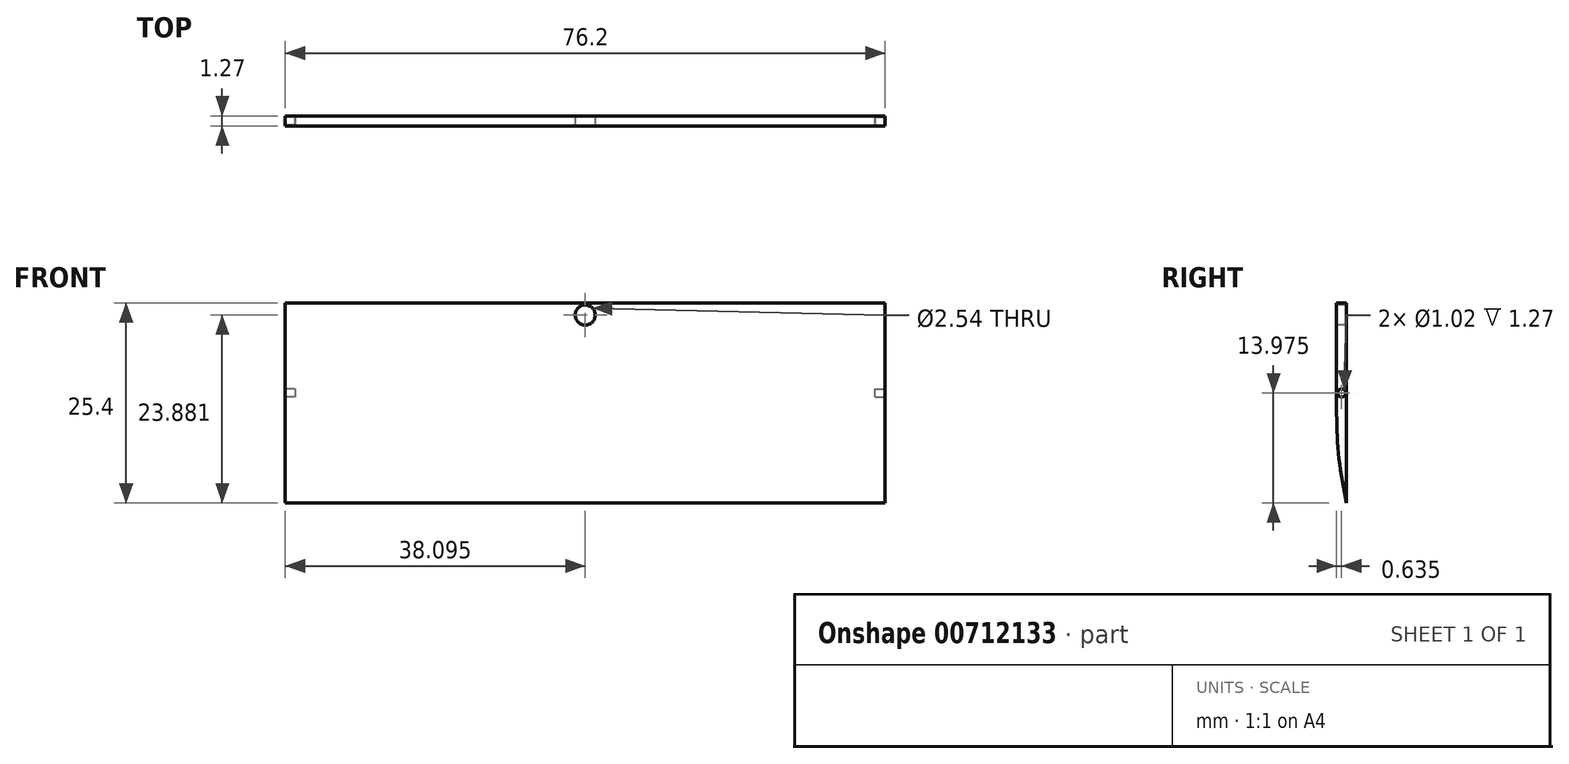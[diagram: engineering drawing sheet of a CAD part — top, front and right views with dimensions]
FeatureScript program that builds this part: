
annotation { "Feature Type Name" : "Feature", "Feature Type Description" : "" }
export const myFeature = defineFeature(function(context is Context, id is Id, definition is map)
    precondition{}
    {
        {
            var Q0;
            Q0=qCreatedBy(makeId("Front.planeOp"),FACE);
            var sketch = newSketch(context, id + "F0", { "sketchPlane" : qUnion([Q0])});
            skLineSegment(sketch, "E0.bottom", {"start": v(9.43, 30.4) * mm, "end": v(-66.77, 30.4) * mm});
            skLineSegment(sketch, "E0.top", {"start": v(9.43, 55.8) * mm, "end": v(-66.77, 55.8) * mm});
            skLineSegment(sketch, "E0.left", {"start": v(9.43, 30.4) * mm, "end": v(9.43, 55.8) * mm});
            skLineSegment(sketch, "E0.right", {"start": v(-66.77, 30.4) * mm, "end": v(-66.77, 55.8) * mm});
            skPoint(sketch, "E0.middle", {"position": v(-28.67, 43.1) * mm});
            skSolve(sketch);
        }
        {
            var Q0;
            Q0=makeQuery(id+"F0.imprint","IMPRINT",FACE,{"disambiguationData":[TD([[makeQuery(id+"F0.imprint","IMPRINT",EDGE,{"derivedFrom":sQuery(id+"F0.wireOp",EDGE,"E0.bottom")}),-1.0]])]});
            extrude(context, id + "F1", {"entities" : qUnion([Q0]), "depth" : 1.27 * mm, "offsetDistance" : 25.4 * mm});
        }
        {
            var Q0;
            Q0=makeQuery(id+"F1.opExtrude","CAP_EDGE",EDGE,{"disambiguationData":[OSD([sQuery(id+"F0.wireOp",EDGE,"E0.bottom")])],"isStart":false});
            fillet(context, id + "F2", {"entities" : qUnion([Q0]), "radius" : 50.8 * mm, "tangentPropagation" : true, "allowEdgeOverflow" : false});
        }
        {
            var Q0;
            Q0=makeQuery(id+"F1.opExtrude","SWEPT_FACE",FACE,{"disambiguationData":[OSD([sQuery(id+"F0.wireOp",EDGE,"E0.right")])]});
            var sketch = newSketch(context, id + "F3", { "sketchPlane" : qUnion([Q0])});
            skCircle(sketch, "E1", {"center": v(0.64, 44.37) * mm, "radius": 0.5 * mm});
            skSolve(sketch);
        }
        {
            var Q0;
            Q0=makeQuery(id+"F3.imprint","IMPRINT",FACE,{"disambiguationData":[TD([[makeQuery(id+"F3.imprint","IMPRINT",EDGE,{"derivedFrom":sQuery(id+"F3.wireOp",EDGE,"E1")}),1.0]])]});
            extrude(context, id + "F4", {"entities" : qUnion([Q0]), "operationType" : NewBodyOperationType.REMOVE, "oppositeDirection" : true, "depth" : 1.27 * mm, "offsetDistance" : 25.4 * mm});
        }
        {
            var Q0;
            Q0=makeQuery(id+"F1.opExtrude","SWEPT_FACE",FACE,{"disambiguationData":[OSD([sQuery(id+"F0.wireOp",EDGE,"E0.left")])]});
            var sketch = newSketch(context, id + "F5", { "sketchPlane" : qUnion([Q0])});
            skCircle(sketch, "E2", {"center": v(-0.64, 44.37) * mm, "radius": 0.5 * mm});
            skSolve(sketch);
        }
        {
            var Q0;
            Q0=makeQuery(id+"F5.imprint","IMPRINT",FACE,{"disambiguationData":[TD([[makeQuery(id+"F5.imprint","IMPRINT",EDGE,{"derivedFrom":sQuery(id+"F5.wireOp",EDGE,"E2")}),1.0]])]});
            extrude(context, id + "F6", {"entities" : qUnion([Q0]), "operationType" : NewBodyOperationType.REMOVE, "oppositeDirection" : true, "depth" : 1.27 * mm, "offsetDistance" : 25.4 * mm});
        }
        {
            var Q0;
            Q0=makeQuery(id+"F1.opExtrude","CAP_FACE",FACE,{"disambiguationData":[OSD([sQuery(id+"F0.wireOp",EDGE,"E0.bottom"),sQuery(id+"F0.wireOp",EDGE,"E0.top"),sQuery(id+"F0.wireOp",EDGE,"E0.left"),sQuery(id+"F0.wireOp",EDGE,"E0.right")])],"isStart":false});
            var sketch = newSketch(context, id + "F7", { "sketchPlane" : qUnion([Q0])});
            skCircle(sketch, "E3", {"center": v(-28.67, 54.28) * mm, "radius": 1.27 * mm});
            skPoint(sketch, "E3.centerSnap0", {"position": v(-28.67, 55.8) * mm});
            skSolve(sketch);
        }
        {
            var Q0;
            Q0=makeQuery(id+"F7.imprint","IMPRINT",FACE,{"disambiguationData":[TD([[makeQuery(id+"F7.imprint","IMPRINT",EDGE,{"derivedFrom":sQuery(id+"F7.wireOp",EDGE,"E3")}),1.0]])]});
            extrude(context, id + "F8", {"entities" : qUnion([Q0]), "operationType" : NewBodyOperationType.REMOVE, "oppositeDirection" : true, "depth" : 25.4 * mm, "offsetDistance" : 25.4 * mm});
        }
    });
